# Revit family: METALFIRE_AVENUE_MF_GHE_T
name_source: partatom
category: Mechanical Equipment
revit_build: Autodesk Revit 2017 (Build: 20160225_1515(x64)
units: mm (PartAtom-declared; Revit-internal decimal feet)

## family parameters
Always vertical = Yes
Cut with Voids When Loaded = No
Host = Wall
OmniClass Number = 23.75.00.00
OmniClass Title = Climate Control (HVAC)
Part Type = Normal
Room Calculation Point = Yes
Round Connector Dimension = Use Diameter
Shared = No

## types (2) — shared parameters
BIM BADGE = https://bim.archiproducts.com
Description = The Avenue represents the gas-fired high efficiency closed fireplaces in the Metalfire range.
ENERGY EFFICIENCY CLASS = B
FINISHING MATERIAL = Black painted vermiculite plates - Metalfire
FRAME MATERIAL = Iron - Metalfire
MATERIAL DESCRIPTION = Iron, galvanized steel and vermiculite plates
Manufacturer = Metalfire
Model = Avenue
OVERALL DEPTH = 488 mm
PRODUCT SHEET = https://www.archiproducts.com
SMOKE EXHAUST = Ø130/200 mm
TECHNICAL SHEET = https://www.metalfire.eu
URL = https://www.metalfire.eu
WEIGHT = 100.00 kg

## per-type parameters (varying)
| type | EFFICIENCY | HEIGHT | OUTPUT | OVERALL HEIGHT | OVERALL WIDTH | PRODUCT CODE | WIDTH |
| 900 x 600 mm | 84.50% | 590 mm | 8.4 kW | 1010 mm | 1073 mm | MF 900-60 GHE T | 900 mm |
| 1050 x 400 mm | 84.00% | 390 mm | 8.3 kW | 778 mm | 1223 mm | MF 1050-40 GHE T | 1050 mm |

## geometry (parser evidence)
native form markers: Sweep x4
no freeform markers — native parametric forms only
